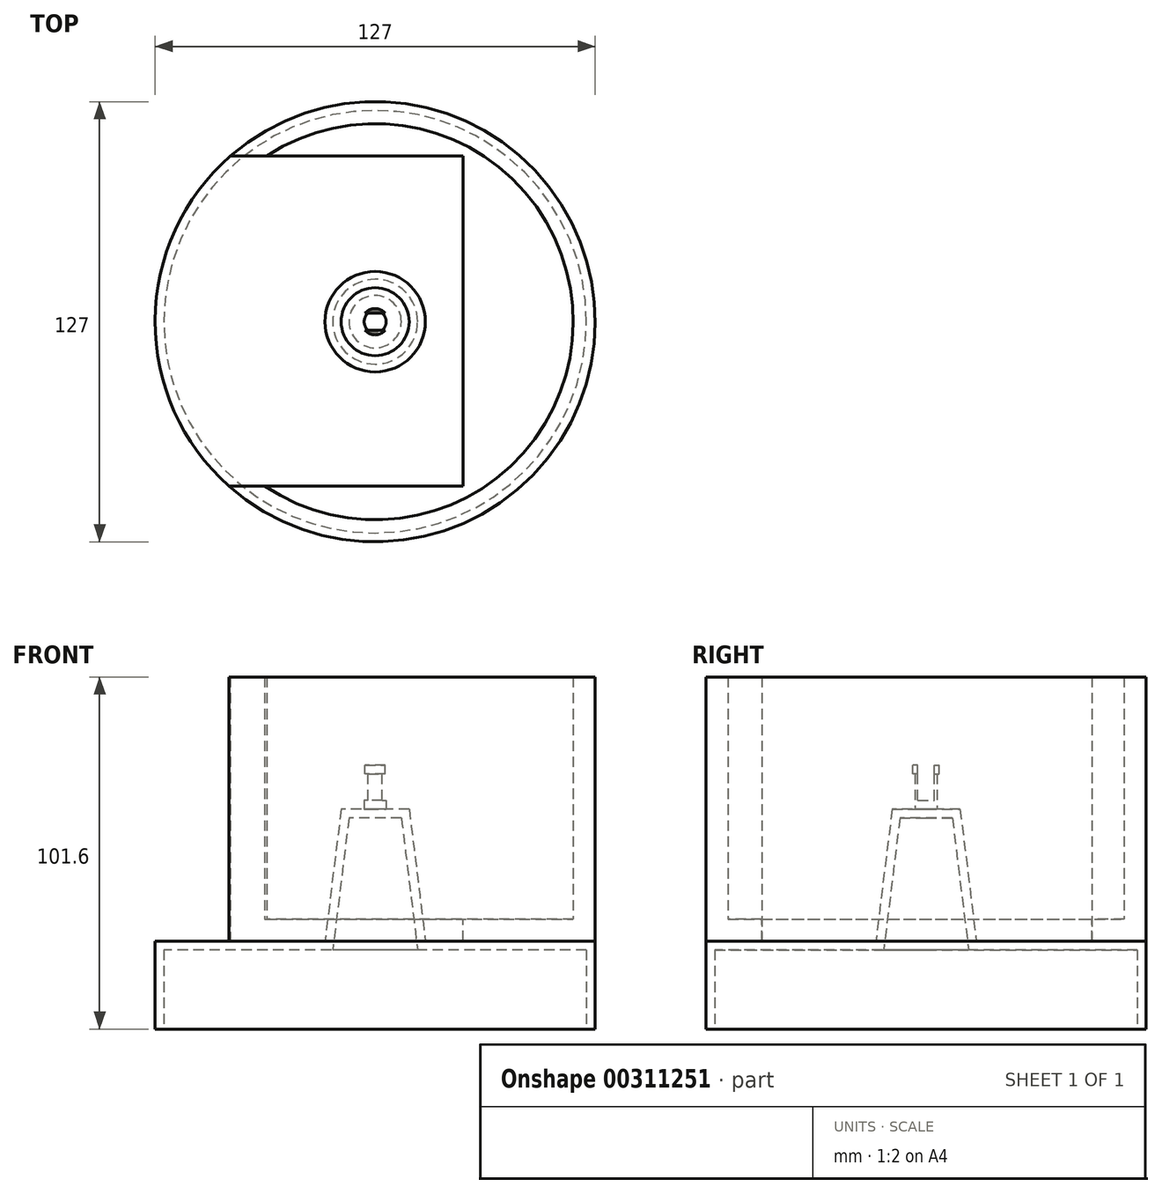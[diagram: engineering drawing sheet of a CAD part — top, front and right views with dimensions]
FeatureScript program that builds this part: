
annotation { "Feature Type Name" : "Feature", "Feature Type Description" : "" }
export const myFeature = defineFeature(function(context is Context, id is Id, definition is map)
    precondition{}
    {
        {
            var Q0;
            Q0=qCreatedBy(makeId("Top.planeOp"),FACE);
            var sketch = newSketch(context, id + "F0", { "sketchPlane" : qUnion([Q0])});
            skCircle(sketch, "E0", {"center": v(0, 0) * mm, "radius": 63.5 * mm});
            skSolve(sketch);
        }
        {
            var Q0;
            Q0=makeQuery(id+"F0.imprint","IMPRINT",FACE,{"disambiguationData":[TD([[makeQuery(id+"F0.imprint","IMPRINT",EDGE,{"derivedFrom":sQuery(id+"F0.wireOp",EDGE,"E0")}),1.0]])]});
            extrude(context, id + "F1", {"entities" : qUnion([Q0]), "depth" : 25.4 * mm});
        }
        {
            var Q0;
            Q0=makeQuery(id+"F1.opExtrude","CAP_FACE",FACE,{"disambiguationData":[OSD([sQuery(id+"F0.wireOp",EDGE,"E0")])],"isStart":false});
            cPlane(context, id + "F2", {"entities" : qUnion([Q0]), "cplaneType" : CPlaneType.OFFSET, "offset" : 0 * mm, "width" : 152.4 * mm, "height" : 152.4 * mm});
        }
        {
            var Q0;
            Q0=qCreatedBy(id+"F2.planeOp",FACE);
            var sketch = newSketch(context, id + "F3", { "sketchPlane" : qUnion([Q0])});
            skCircle(sketch, "E1", {"center": v(0, 0) * mm, "radius": 63.5 * mm});
            skSolve(sketch);
        }
        {
            var Q0;
            Q0=makeQuery(id+"F3.imprint","IMPRINT",FACE,{"disambiguationData":[TD([[makeQuery(id+"F3.imprint","IMPRINT",EDGE,{"derivedFrom":sQuery(id+"F3.wireOp",EDGE,"E1")}),1.0]])]});
            extrude(context, id + "F4", {"entities" : qUnion([Q0]), "depth" : 76.2 * mm});
        }
        {
            var Q0;
            Q0=qCreatedBy(makeId("Front.planeOp"),FACE);
            cPlane(context, id + "F5", {"entities" : qUnion([Q0]), "cplaneType" : CPlaneType.OFFSET, "offset" : 63.5 * mm, "width" : 152.4 * mm, "height" : 152.4 * mm});
        }
        {
            var Q0;
            Q0=qCreatedBy(id+"F5.planeOp",FACE);
            var sketch = newSketch(context, id + "F6", { "sketchPlane" : qUnion([Q0])});
            skLineSegment(sketch, "E2", {"start": v(0, 25.4) * mm, "end": v(0, 0) * mm, "construction": true});
            skLineSegment(sketch, "E3", {"start": v(0, 25.4) * mm, "end": v(63.5, 25.4) * mm, "construction": true});
            skLineSegment(sketch, "E4", {"start": v(0, 25.4) * mm, "end": v(-63.5, 25.4) * mm, "construction": true});
            skLineSegment(sketch, "E5", {"start": v(0, 25.4) * mm, "end": v(-31.75, 25.4) * mm, "construction": true});
            skLineSegment(sketch, "E6", {"start": v(0, 25.4) * mm, "end": v(31.75, 25.4) * mm, "construction": true});
            skLineSegment(sketch, "E7", {"start": v(-63.5, 25.4) * mm, "end": v(-31.75, 25.4) * mm, "construction": true});
            skLineSegment(sketch, "E8", {"start": v(-31.75, 25.4) * mm, "end": v(-47.62, 25.4) * mm, "construction": true});
            skLineSegment(sketch, "E9", {"start": v(31.75, 25.4) * mm, "end": v(63.5, 25.4) * mm, "construction": true});
            skLineSegment(sketch, "E10", {"start": v(47.62, 25.4) * mm, "end": v(63.5, 25.4) * mm, "construction": true});
            skLineSegment(sketch, "E11", {"start": v(-47.62, 25.4) * mm, "end": v(-47.62, 101.6) * mm});
            skLineSegment(sketch, "E12", {"start": v(31.75, 25.4) * mm, "end": v(31.75, 101.6) * mm});
            skLineSegment(sketch, "E13", {"start": v(31.75, 101.6) * mm, "end": v(-47.62, 101.6) * mm});
            skLineSegment(sketch, "E14", {"start": v(-47.62, 25.4) * mm, "end": v(31.75, 25.4) * mm});
            skSolve(sketch);
        }
        {
            var Q0;
            Q0=makeQuery(id+"F4.opExtrude","CAP_FACE",FACE,{"disambiguationData":[OSD([sQuery(id+"F3.wireOp",EDGE,"E1")])],"isStart":false});
            shell(context, id + "F7", {"entities" : qUnion([Q0]), "thickness" : 6.35 * mm});
        }
        {
            var Q0;
            Q0=qCreatedBy(makeId("Front.planeOp"),FACE);
            cPlane(context, id + "F8", {"entities" : qUnion([Q0]), "cplaneType" : CPlaneType.OFFSET, "offset" : 63.5 * mm, "oppositeDirection" : true, "width" : 152.4 * mm, "height" : 152.4 * mm});
        }
        {
            var Q0;
            Q0=qCreatedBy(makeId("Right.planeOp"),FACE);
            cPlane(context, id + "F9", {"entities" : qUnion([Q0]), "cplaneType" : CPlaneType.OFFSET, "offset" : 63.5 * mm, "oppositeDirection" : true, "width" : 152.4 * mm, "height" : 152.4 * mm});
        }
        {
            var Q0;
            Q0=qCreatedBy(id+"F9.planeOp",FACE);
            var sketch = newSketch(context, id + "F10", { "sketchPlane" : qUnion([Q0])});
            skLineSegment(sketch, "E15", {"start": v(0, 25.4) * mm, "end": v(0, 0) * mm, "construction": true});
            skLineSegment(sketch, "E16", {"start": v(0, 25.4) * mm, "end": v(63.8, 25.4) * mm, "construction": true});
            skLineSegment(sketch, "E17", {"start": v(0, 25.4) * mm, "end": v(-63.2, 25.4) * mm, "construction": true});
            skLineSegment(sketch, "E18", {"start": v(0, 25.4) * mm, "end": v(31.9, 25.4) * mm, "construction": true});
            skLineSegment(sketch, "E19", {"start": v(31.9, 25.4) * mm, "end": v(-31.6, 25.4) * mm, "construction": true});
            skLineSegment(sketch, "E20", {"start": v(-31.6, 25.4) * mm, "end": v(-63.2, 25.4) * mm, "construction": true});
            skLineSegment(sketch, "E21", {"start": v(-47.4, 25.4) * mm, "end": v(-31.6, 25.4) * mm, "construction": true});
            skLineSegment(sketch, "E22", {"start": v(31.9, 25.4) * mm, "end": v(63.8, 25.4) * mm, "construction": true});
            skLineSegment(sketch, "E23", {"start": v(47.85, 25.4) * mm, "end": v(31.9, 25.4) * mm, "construction": true});
            skLineSegment(sketch, "E24", {"start": v(47.85, 25.4) * mm, "end": v(47.85, 101.6) * mm});
            skLineSegment(sketch, "E25", {"start": v(-47.4, 25.4) * mm, "end": v(-47.4, 101.6) * mm});
            skLineSegment(sketch, "E26", {"start": v(-47.4, 101.6) * mm, "end": v(47.85, 101.6) * mm});
            skLineSegment(sketch, "E27", {"start": v(47.85, 25.4) * mm, "end": v(-47.4, 25.4) * mm});
            skSolve(sketch);
        }
        {
            var Q0;
            Q0 = qSketchRegion(id + "F10", true);
            extrude(context, id + "F11", {"entities" : qUnion([Q0]), "operationType" : NewBodyOperationType.REMOVE, "depth" : 88.9 * mm});
        }
        {
            var Q0;
            Q0=qCreatedBy(id+"F2.planeOp",FACE);
            var sketch = newSketch(context, id + "F12", { "sketchPlane" : qUnion([Q0])});
            skCircle(sketch, "E28", {"center": v(0, 0) * mm, "radius": 14.49 * mm});
            skSolve(sketch);
        }
        {
            var Q0;
            Q0 = qSketchRegion(id + "F12", true);
            extrude(context, id + "F13", {"entities" : qUnion([Q0]), "operationType" : NewBodyOperationType.ADD, "depth" : 38.1 * mm, "hasDraft" : true, "draftAngle" : 7 * degree, "draftPullDirection" : true});
        }
        {
            var Q0;
            Q0=makeQuery(id+"F1.opExtrude","CAP_FACE",FACE,{"disambiguationData":[OSD([sQuery(id+"F0.wireOp",EDGE,"E0")])],"isStart":true});
            shell(context, id + "F14", {"entities" : qUnion([Q0]), "thickness" : 2.54 * mm});
        }
        {
            var Q0;
            Q0=makeQuery(id+"F13.opExtrude","CAP_FACE",FACE,{"disambiguationData":[OSD([sQuery(id+"F12.wireOp",EDGE,"E28")])],"isStart":false});
            var sketch = newSketch(context, id + "F15", { "sketchPlane" : qUnion([Q0])});
            skCircle(sketch, "E29", {"center": v(0, 0) * mm, "radius": 3.18 * mm});
            skSolve(sketch);
        }
        {
            var Q0;
            Q0 = qSketchRegion(id + "F15", true);
            extrude(context, id + "F16", {"entities" : qUnion([Q0]), "operationType" : NewBodyOperationType.ADD, "depth" : 12.7 * mm});
        }
        {
            var Q0;
            Q0=makeQuery(id+"F16.opExtrude","CAP_FACE",FACE,{"disambiguationData":[OSD([sQuery(id+"F15.wireOp",EDGE,"E29")])],"isStart":false});
            var sketch = newSketch(context, id + "F17", { "sketchPlane" : qUnion([Q0])});
            skCircle(sketch, "E30", {"center": v(0, 0) * mm, "radius": 3.81 * mm});
            skLineSegment(sketch, "E31.bottom", {"start": v(2.92, -2.45) * mm, "end": v(-2.92, -2.45) * mm});
            skLineSegment(sketch, "E31.top", {"start": v(2.92, 2.45) * mm, "end": v(-2.92, 2.45) * mm});
            skLineSegment(sketch, "E31.left", {"start": v(2.92, -2.45) * mm, "end": v(2.92, 2.45) * mm});
            skLineSegment(sketch, "E31.right", {"start": v(-2.92, -2.45) * mm, "end": v(-2.92, 2.45) * mm});
            skCircle(sketch, "E32", {"center": v(0, 0) * mm, "radius": 3.18 * mm});
            skSolve(sketch);
        }
        {
            var Q0;
            Q0 = qSketchRegion(id + "F17", true);
            extrude(context, id + "F18", {"entities" : qUnion([Q0]), "operationType" : NewBodyOperationType.ADD, "oppositeDirection" : true, "depth" : 2.54 * mm});
        }
        {
            var Q0;
            {var subQ0=sQuery(id+"F17.wireOp",EDGE,"E32");var subQ7=sQuery(id+"F17.wireOp",EDGE,"E31.bottom");var subQ8=makeQuery(id+"F17.imprint","INTERSECT",VERTEX,{"disambiguationData":[OD(0.0)],"derivedFrom":[subQ7,subQ0]});Q0=makeQuery(id+"F17.imprint","IMPRINT",FACE,{"disambiguationData":[TD([[makeQuery(id+"F17.imprint","IMPRINT",EDGE,{"disambiguationData":[TD([[subQ8,-1.0]])],"derivedFrom":subQ7}),-1.0]])]});}
            var Q1;
            {var subQ0=sQuery(id+"F17.wireOp",EDGE,"E32");var subQ1=sQuery(id+"F17.wireOp",EDGE,"E31.left");var subQ2=makeQuery(id+"F17.imprint","INTERSECT",VERTEX,{"disambiguationData":[OD(0.0)],"derivedFrom":[subQ1,subQ0]});Q1=makeQuery(id+"F17.imprint","IMPRINT",FACE,{"disambiguationData":[TD([[makeQuery(id+"F17.imprint","IMPRINT",EDGE,{"disambiguationData":[TD([[subQ2,-1.0]])],"derivedFrom":subQ1}),-1.0]])]});}
            var Q2;
            {var subQ0=sQuery(id+"F17.wireOp",EDGE,"E32");var subQ1=sQuery(id+"F17.wireOp",EDGE,"E31.right");var subQ2=makeQuery(id+"F17.imprint","INTERSECT",VERTEX,{"disambiguationData":[OD(0.0)],"derivedFrom":[subQ1,subQ0]});Q2=makeQuery(id+"F17.imprint","IMPRINT",FACE,{"disambiguationData":[TD([[makeQuery(id+"F17.imprint","IMPRINT",EDGE,{"disambiguationData":[TD([[subQ2,-1.0]])],"derivedFrom":subQ1}),1.0]])]});}
            extrude(context, id + "F19", {"entities" : qUnion([Q0, Q1, Q2]), "operationType" : NewBodyOperationType.REMOVE, "oppositeDirection" : true, "depth" : 10.16 * mm});
        }
        {
            var Q0;
            {var subQ1=sQuery(id+"F17.wireOp",EDGE,"E31.bottom");var subQ3=sQuery(id+"F17.wireOp",EDGE,"E32");var subQ4=makeQuery(id+"F17.imprint","INTERSECT",VERTEX,{"disambiguationData":[OD(1.0)],"derivedFrom":[subQ1,subQ3]});Q0=makeQuery(id+"F17.imprint","IMPRINT",FACE,{"disambiguationData":[TD([[makeQuery(id+"F17.imprint","IMPRINT",EDGE,{"disambiguationData":[TD([[subQ4,1.0]])],"derivedFrom":subQ3}),-1.0]])]});}
            var Q1;
            {var subQ1=sQuery(id+"F17.wireOp",EDGE,"E31.top");var subQ3=sQuery(id+"F17.wireOp",EDGE,"E32");var subQ4=makeQuery(id+"F17.imprint","INTERSECT",VERTEX,{"disambiguationData":[OD(1.0)],"derivedFrom":[subQ1,subQ3]});Q1=makeQuery(id+"F17.imprint","IMPRINT",FACE,{"disambiguationData":[TD([[makeQuery(id+"F17.imprint","IMPRINT",EDGE,{"disambiguationData":[TD([[subQ4,-1.0]])],"derivedFrom":subQ3}),-1.0]])]});}
            var Q2;
            {var subQ1=sQuery(id+"F17.wireOp",EDGE,"E31.bottom");var subQ3=sQuery(id+"F17.wireOp",EDGE,"E32");var subQ4=makeQuery(id+"F17.imprint","INTERSECT",VERTEX,{"disambiguationData":[OD(0.0)],"derivedFrom":[subQ1,subQ3]});Q2=makeQuery(id+"F17.imprint","IMPRINT",FACE,{"disambiguationData":[TD([[makeQuery(id+"F17.imprint","IMPRINT",EDGE,{"disambiguationData":[TD([[subQ4,-1.0]])],"derivedFrom":subQ3}),-1.0]])]});}
            var Q3;
            {var subQ1=sQuery(id+"F17.wireOp",EDGE,"E31.top");var subQ3=sQuery(id+"F17.wireOp",EDGE,"E32");var subQ4=makeQuery(id+"F17.imprint","INTERSECT",VERTEX,{"disambiguationData":[OD(0.0)],"derivedFrom":[subQ1,subQ3]});Q3=makeQuery(id+"F17.imprint","IMPRINT",FACE,{"disambiguationData":[TD([[makeQuery(id+"F17.imprint","IMPRINT",EDGE,{"disambiguationData":[TD([[subQ4,1.0]])],"derivedFrom":subQ3}),-1.0]])]});}
            var Q4;
            {var subQ0=sQuery(id+"F17.wireOp",EDGE,"E31.right");var subQ4=sQuery(id+"F17.wireOp",EDGE,"E32");var subQ5=makeQuery(id+"F17.imprint","INTERSECT",VERTEX,{"disambiguationData":[OD(0.0)],"derivedFrom":[subQ0,subQ4]});Q4=makeQuery(id+"F17.imprint","IMPRINT",FACE,{"disambiguationData":[TD([[makeQuery(id+"F17.imprint","IMPRINT",EDGE,{"disambiguationData":[TD([[subQ5,1.0]])],"derivedFrom":subQ4}),-1.0]])]});}
            var Q5;
            {var subQ0=sQuery(id+"F17.wireOp",EDGE,"E31.left");var subQ4=sQuery(id+"F17.wireOp",EDGE,"E32");var subQ5=makeQuery(id+"F17.imprint","INTERSECT",VERTEX,{"disambiguationData":[OD(0.0)],"derivedFrom":[subQ0,subQ4]});Q5=makeQuery(id+"F17.imprint","IMPRINT",FACE,{"disambiguationData":[TD([[makeQuery(id+"F17.imprint","IMPRINT",EDGE,{"disambiguationData":[TD([[subQ5,-1.0]])],"derivedFrom":subQ4}),-1.0]])]});}
            extrude(context, id + "F20", {"entities" : qUnion([Q0, Q1, Q2, Q3, Q4, Q5]), "operationType" : NewBodyOperationType.REMOVE, "oppositeDirection" : true, "depth" : 10.16 * mm});
        }
    });
